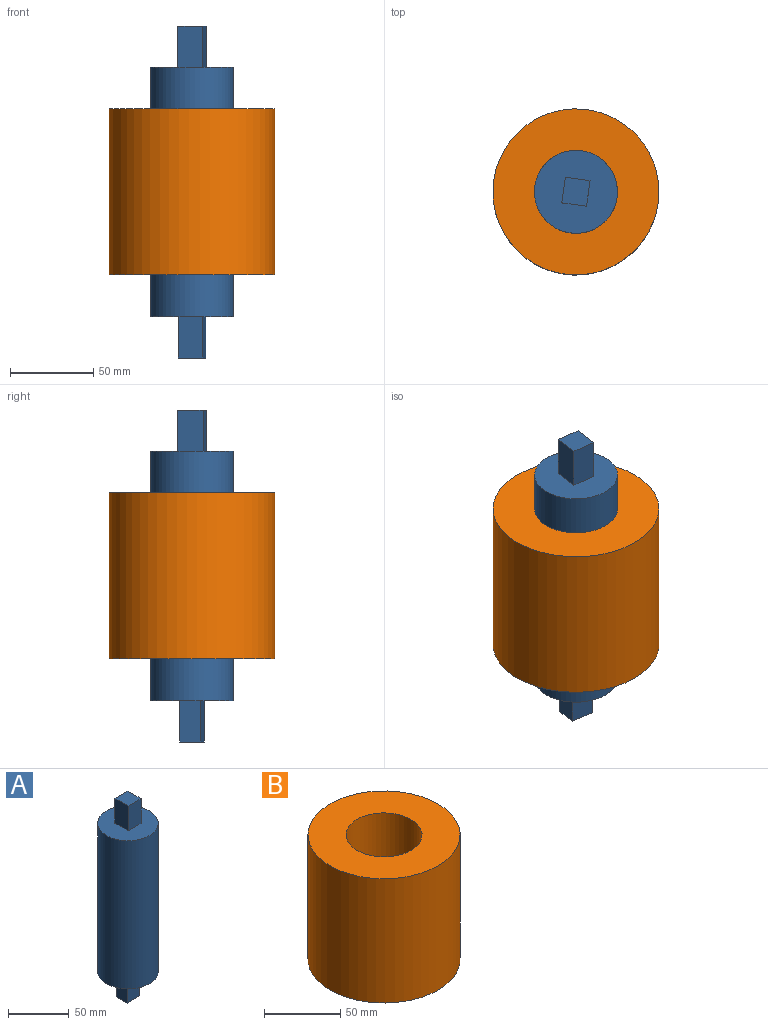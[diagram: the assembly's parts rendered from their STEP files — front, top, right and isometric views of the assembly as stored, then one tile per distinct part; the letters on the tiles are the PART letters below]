
ASSEMBLY  parts=2 mates=1
PART A: 13 faces, bbox 50x50x200 mm
  f0: plane 50x50mm, normal (0,0,-1), area 1773.8mm2, adj f1,f8,f9,f10,f11
  f1: cylinder r=25mm len=150mm, axis (0,0,-1), area 23561.9mm2, adj f0,f2
  f2: plane 50x50mm, normal (0,0,1), area 1730.3mm2, adj f1,f3,f4,f5,f6
  f3: plane 25x15.55mm, normal (1,0,0), area 388.6mm2, adj f2,f4,f6,f7
  f4: plane 25x15mm, normal (0,1,0), area 375mm2, adj f2,f3,f5,f7
  f5: plane 25x15.55mm, normal (-1,0,0), area 388.6mm2, adj f2,f4,f6,f7
  f6: plane 25x15mm, normal (0,-1,0), area 375mm2, adj f2,f3,f5,f7
  f7: plane 15.55x15mm, normal (0,0,1), area 233.2mm2, adj f3,f4,f5,f6
  f8: plane 25x12.65mm, normal (1,0,0), area 316.2mm2, adj f0,f9,f11,f12
  f9: plane 25x15mm, normal (0,-1,0), area 375mm2, adj f0,f8,f10,f12
  f10: plane 25x12.65mm, normal (-1,0,0), area 316.2mm2, adj f0,f9,f11,f12
  f11: plane 25x15mm, normal (0,1,0), area 375mm2, adj f0,f8,f10,f12
  f12: plane 15x12.65mm, normal (0,0,-1), area 189.7mm2, adj f8,f9,f10,f11
PART B: 4 faces, bbox 100x100x100 mm
  f0: cylinder r=50mm len=100mm, axis (0,0,-1), area 31415.9mm2, adj f1,f2
  f1: plane 100x100mm, normal (0,0,1), area 5890.5mm2, adj f0,f3
  f2: plane 100x100mm, normal (0,0,-1), area 5890.5mm2, adj f0,f3
  f3: cylinder r=25mm len=100mm, axis (0,0,1), area 15708mm2, adj f1,f2
PLACE A rot(axis=(0,0,-1),7.9deg) t=(-10,13.87,-45.54)mm
PLACE B t=(-10,13.87,-20.54)mm fixed
MATE revolute B.f0 <-> A.f1  axis (0,0,1) through (-10,13.87,29.46)mm
